# Revit family: 1378002 Cromarty 100  BSS
name_source: partatom
category: Lighting Fixtures
revit_build: Autodesk Revit 2018 (Build: 20170223_1515(x64)
units: mm (PartAtom-declared; Revit-internal decimal feet)

## family parameters
Always vertical = Yes
Cut with Voids When Loaded = No
Light Source = Yes
OmniClass Number = 23.80.70.00
OmniClass Title = Lighting
Part Type = Normal
Room Calculation Point = No
Round Connector Dimension = Use Diameter
Shared = No
Work Plane-Based = No

## types (1)
- 1378002 - Cromarty 100 LED - Brushed Stainless Steel - Ground Light
    Apparent Load = 9 VA
    Color Filter = 16777215
    Dimmable = No
    Dimming Lamp Color Temperature Shift = <None>
    Driver Included = Yes
    Driver Required = No
    Efficacy (lm/W) = 59
    Electrical Class = 1
    Emit from Line Length = 610 mm
    Lamp = LED
    Length of Cable Supplied = 1300MM
    Light Source Fixed = Yes
    Location Rating = IP67
    Main Finish = Brushed Stainless Steel
    Main Material = Stainless Steel 316
    Photometric Web File = GNC-19586  7882 - Cromarty LED  ies.ies
    Power (W) = 8.6
    Product Location = Outdoor/Ground
    Product Name = Cromarty 100 LED
    Product SKU = 1378002
    Product URL = https://www.astrolighting.com
    Tilt Angle = 60.00°

## geometry (parser evidence)
native form markers: Sweep x1
no freeform markers — native parametric forms only
